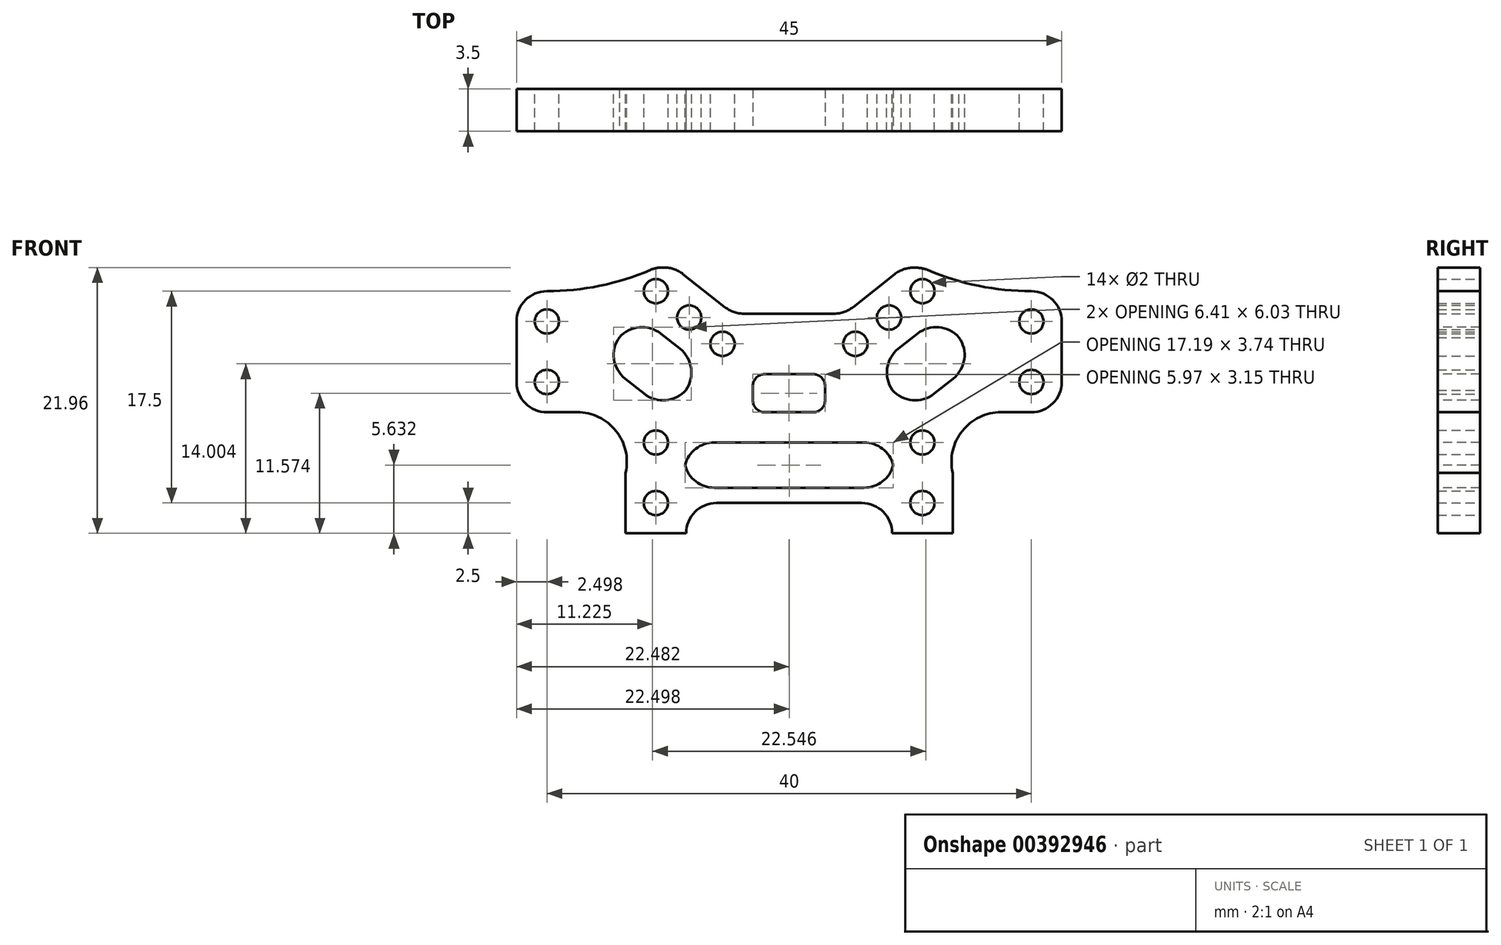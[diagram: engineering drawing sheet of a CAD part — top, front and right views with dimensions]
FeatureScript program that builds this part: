
annotation { "Feature Type Name" : "Feature", "Feature Type Description" : "" }
export const myFeature = defineFeature(function(context is Context, id is Id, definition is map)
    precondition{}
    {
        {
            var Q0;
            Q0=qCreatedBy(makeId("Front.planeOp"),FACE);
            var sketch = newSketch(context, id + "F0", { "sketchPlane" : qUnion([Q0])});
            skCircle(sketch, "E0", {"center": v(-2.32, 0) * mm, "radius": 1 * mm});
            skCircle(sketch, "E1", {"center": v(19.68, 0) * mm, "radius": 1 * mm});
            skCircle(sketch, "E2", {"center": v(-2.32, 5) * mm, "radius": 1 * mm});
            skCircle(sketch, "E3", {"center": v(19.68, 5) * mm, "radius": 1 * mm});
            skCircle(sketch, "E4", {"center": v(-11.32, 10) * mm, "radius": 1 * mm});
            skCircle(sketch, "E5", {"center": v(-11.32, 15) * mm, "radius": 1 * mm});
            skPoint(sketch, "E6.endSnap0", {"position": v(8.68, 5) * mm});
            skCircle(sketch, "E7.MirrorC", {"center": v(28.68, 15) * mm, "radius": 1 * mm});
            skCircle(sketch, "E8.MirrorC", {"center": v(28.68, 10) * mm, "radius": 1 * mm});
            skLineSegment(sketch, "E9", {"start": v(-4.82, 0) * mm, "end": v(-4.82, -2.5) * mm});
            skLineSegment(sketch, "E10", {"start": v(-4.82, -2.5) * mm, "end": v(0.18, -2.5) * mm});
            skLineSegment(sketch, "E11", {"start": v(0.18, -2.5) * mm, "end": v(0.18, 0) * mm});
            skLineSegment(sketch, "E12.trimOffspring", {"start": v(0.18, 0) * mm, "end": v(8.68, 0) * mm});
            skLineSegment(sketch, "E13.trimOffspring", {"start": v(18.68, 0) * mm, "end": v(19.68, 0) * mm});
            skLineSegment(sketch, "E14", {"start": v(-11.32, 10) * mm, "end": v(-13.82, 10) * mm});
            skLineSegment(sketch, "E15", {"start": v(-13.82, 10) * mm, "end": v(-13.82, 7.5) * mm});
            skLineSegment(sketch, "E16", {"start": v(-13.82, 7.5) * mm, "end": v(-8.82, 7.5) * mm});
            skLineSegment(sketch, "E17", {"start": v(-4.82, 0) * mm, "end": v(-4.82, 2.5) * mm});
            skArc(sketch, "E18", {"start": v(-4.82, 2.5) * mm, "mid": v(-5.62, 5.96) * mm, "end": v(-8.82, 7.5) * mm});
            skLineSegment(sketch, "E19", {"start": v(-11.32, 17.5) * mm, "end": v(-13.82, 17.5) * mm});
            skLineSegment(sketch, "E20", {"start": v(-13.82, 17.5) * mm, "end": v(-13.82, 10) * mm});
            skLineSegment(sketch, "E21.MirrorCS", {"start": v(28.68, 17.5) * mm, "end": v(31.18, 17.5) * mm});
            skLineSegment(sketch, "E22.MirrorCS", {"start": v(31.18, 17.5) * mm, "end": v(31.18, 10) * mm});
            skLineSegment(sketch, "E23.MirrorCS", {"start": v(31.18, 10) * mm, "end": v(31.18, 7.5) * mm});
            skLineSegment(sketch, "E24.MirrorCS", {"start": v(31.18, 7.5) * mm, "end": v(26.18, 7.5) * mm});
            skArc(sketch, "E25.MirrorCS", {"start": v(22.18, 2.5) * mm, "mid": v(22.98, 5.96) * mm, "end": v(26.18, 7.5) * mm});
            skLineSegment(sketch, "E26.MirrorCS", {"start": v(22.18, 0) * mm, "end": v(22.18, 2.5) * mm});
            skLineSegment(sketch, "E27.MirrorCS", {"start": v(22.18, 0) * mm, "end": v(22.18, -2.5) * mm});
            skLineSegment(sketch, "E28.MirrorCS", {"start": v(22.18, -2.5) * mm, "end": v(17.18, -2.5) * mm});
            skLineSegment(sketch, "E29.MirrorCS", {"start": v(17.18, 0) * mm, "end": v(8.68, 0) * mm});
            skLineSegment(sketch, "E30.MirrorCS", {"start": v(17.18, -2.5) * mm, "end": v(17.18, 0) * mm});
            skCircle(sketch, "E31", {"center": v(-2.32, 17.5) * mm, "radius": 1 * mm});
            skCircle(sketch, "E32.MirrorC", {"center": v(19.68, 17.5) * mm, "radius": 1 * mm});
            skCircle(sketch, "E33", {"center": v(3.18, 13.15) * mm, "radius": 1 * mm});
            skCircle(sketch, "E34", {"center": v(14.15, 13.15) * mm, "radius": 1 * mm});
            skCircle(sketch, "E35", {"center": v(16.93, 15.32) * mm, "radius": 1 * mm});
            skCircle(sketch, "E36", {"center": v(0.43, 15.32) * mm, "radius": 1 * mm});
            skLineSegment(sketch, "E37.0", {"start": v(13.28, 15.65) * mm, "end": v(18.07, 19.44) * mm});
            skLineSegment(sketch, "E37.1", {"start": v(4.05, 15.65) * mm, "end": v(13.28, 15.65) * mm});
            skLineSegment(sketch, "E37.2", {"start": v(-0.77, 19.46) * mm, "end": v(4.05, 15.65) * mm});
            skLineSegment(sketch, "E38", {"start": v(-0.77, 19.46) * mm, "end": v(-2.32, 19.46) * mm});
            skLineSegment(sketch, "E39", {"start": v(18.07, 19.44) * mm, "end": v(19.68, 19.44) * mm});
            skArc(sketch, "E40", {"start": v(19.68, 19.44) * mm, "mid": v(24.07, 18) * mm, "end": v(28.68, 17.5) * mm});
            skArc(sketch, "E41", {"start": v(-11.32, 17.5) * mm, "mid": v(-6.72, 18) * mm, "end": v(-2.32, 19.46) * mm});
            skSolve(sketch);
        }
        {
            var Q0;
            Q0 = qSketchRegion(id + "F0", true);
            extrude(context, id + "F1", {"entities" : qUnion([Q0]), "depth" : 3.5 * mm});
        }
        {
            var Q0;
            Q0=makeQuery(id+"F1.opExtrude","SWEPT_EDGE",EDGE,{"disambiguationData":[OSD([sQuery(id+"F0.wireOp",EDGE,"E19"),sQuery(id+"F0.wireOp",EDGE,"E20")])]});
            var Q1;
            Q1=makeQuery(id+"F1.opExtrude","SWEPT_EDGE",EDGE,{"disambiguationData":[OSD([sQuery(id+"F0.wireOp",EDGE,"E15"),sQuery(id+"F0.wireOp",EDGE,"E16")])]});
            var Q2;
            Q2=makeQuery(id+"F1.opExtrude","SWEPT_EDGE",EDGE,{"disambiguationData":[OSD([sQuery(id+"F0.wireOp",EDGE,"E23.MirrorCS"),sQuery(id+"F0.wireOp",EDGE,"E24.MirrorCS")])]});
            var Q3;
            Q3=makeQuery(id+"F1.opExtrude","SWEPT_EDGE",EDGE,{"disambiguationData":[OSD([sQuery(id+"F0.wireOp",EDGE,"E21.MirrorCS"),sQuery(id+"F0.wireOp",EDGE,"E22.MirrorCS")])]});
            var Q4;
            Q4=makeQuery(id+"F1.opExtrude","SWEPT_EDGE",EDGE,{"disambiguationData":[OSD([sQuery(id+"F0.wireOp",EDGE,"E38"),sQuery(id+"F0.wireOp",EDGE,"E41")])]});
            var Q5;
            Q5=makeQuery(id+"F1.opExtrude","SWEPT_EDGE",EDGE,{"disambiguationData":[OSD([sQuery(id+"F0.wireOp",EDGE,"E37.2"),sQuery(id+"F0.wireOp",EDGE,"E38")])]});
            var Q6;
            Q6=makeQuery(id+"F1.opExtrude","SWEPT_EDGE",EDGE,{"disambiguationData":[OSD([sQuery(id+"F0.wireOp",EDGE,"E37.1"),sQuery(id+"F0.wireOp",EDGE,"E37.2")])]});
            var Q7;
            Q7=makeQuery(id+"F1.opExtrude","SWEPT_EDGE",EDGE,{"disambiguationData":[OSD([sQuery(id+"F0.wireOp",EDGE,"E37.0"),sQuery(id+"F0.wireOp",EDGE,"E37.1")])]});
            var Q8;
            Q8=makeQuery(id+"F1.opExtrude","SWEPT_EDGE",EDGE,{"disambiguationData":[OSD([sQuery(id+"F0.wireOp",EDGE,"E37.0"),sQuery(id+"F0.wireOp",EDGE,"E39")])]});
            var Q9;
            Q9=makeQuery(id+"F1.opExtrude","SWEPT_EDGE",EDGE,{"disambiguationData":[OSD([sQuery(id+"F0.wireOp",EDGE,"E39"),sQuery(id+"F0.wireOp",EDGE,"E40")])]});
            var Q10;
            Q10=makeQuery(id+"F1.opExtrude","SWEPT_EDGE",EDGE,{"disambiguationData":[OSD([sQuery(id+"F0.wireOp",EDGE,"E11"),sQuery(id+"F0.wireOp",EDGE,"E12.trimOffspring")])]});
            var Q11;
            Q11=makeQuery(id+"F1.opExtrude","SWEPT_EDGE",EDGE,{"disambiguationData":[OSD([sQuery(id+"F0.wireOp",EDGE,"E29.MirrorCS"),sQuery(id+"F0.wireOp",EDGE,"E30.MirrorCS")])]});
            fillet(context, id + "F2", {"entities" : qUnion([Q0, Q1, Q2, Q3, Q4, Q5, Q6, Q7, Q8, Q9, Q10, Q11]), "radius" : 2.5 * mm, "tangentPropagation" : true, "allowEdgeOverflow" : false});
        }
        {
            var Q0;
            Q0=makeQuery(id+"F1.opExtrude","CAP_FACE",FACE,{"disambiguationData":[OSD([sQuery(id+"F0.wireOp",EDGE,"E0"),sQuery(id+"F0.wireOp",EDGE,"E1"),sQuery(id+"F0.wireOp",EDGE,"E2"),sQuery(id+"F0.wireOp",EDGE,"E3"),sQuery(id+"F0.wireOp",EDGE,"E4"),sQuery(id+"F0.wireOp",EDGE,"E5"),sQuery(id+"F0.wireOp",EDGE,"E7.MirrorC"),sQuery(id+"F0.wireOp",EDGE,"E8.MirrorC"),sQuery(id+"F0.wireOp",EDGE,"E9"),sQuery(id+"F0.wireOp",EDGE,"E10"),sQuery(id+"F0.wireOp",EDGE,"E11"),sQuery(id+"F0.wireOp",EDGE,"E12.trimOffspring"),sQuery(id+"F0.wireOp",EDGE,"E15"),sQuery(id+"F0.wireOp",EDGE,"E16"),sQuery(id+"F0.wireOp",EDGE,"E17"),sQuery(id+"F0.wireOp",EDGE,"E18"),sQuery(id+"F0.wireOp",EDGE,"E19"),sQuery(id+"F0.wireOp",EDGE,"E20"),sQuery(id+"F0.wireOp",EDGE,"E21.MirrorCS"),sQuery(id+"F0.wireOp",EDGE,"E22.MirrorCS"),sQuery(id+"F0.wireOp",EDGE,"E23.MirrorCS"),sQuery(id+"F0.wireOp",EDGE,"E24.MirrorCS"),sQuery(id+"F0.wireOp",EDGE,"E25.MirrorCS"),sQuery(id+"F0.wireOp",EDGE,"E26.MirrorCS"),sQuery(id+"F0.wireOp",EDGE,"E27.MirrorCS"),sQuery(id+"F0.wireOp",EDGE,"E28.MirrorCS"),sQuery(id+"F0.wireOp",EDGE,"E29.MirrorCS"),sQuery(id+"F0.wireOp",EDGE,"E30.MirrorCS"),sQuery(id+"F0.wireOp",EDGE,"E31"),sQuery(id+"F0.wireOp",EDGE,"E32.MirrorC"),sQuery(id+"F0.wireOp",EDGE,"E33"),sQuery(id+"F0.wireOp",EDGE,"E34"),sQuery(id+"F0.wireOp",EDGE,"E35"),sQuery(id+"F0.wireOp",EDGE,"E36"),sQuery(id+"F0.wireOp",EDGE,"E37.0"),sQuery(id+"F0.wireOp",EDGE,"E37.1"),sQuery(id+"F0.wireOp",EDGE,"E37.2"),sQuery(id+"F0.wireOp",EDGE,"E38"),sQuery(id+"F0.wireOp",EDGE,"E39"),sQuery(id+"F0.wireOp",EDGE,"E40"),sQuery(id+"F0.wireOp",EDGE,"E41")])],"isStart":false});
            var sketch = newSketch(context, id + "F3", { "sketchPlane" : qUnion([Q0])});
            skLineSegment(sketch, "E42", {"start": v(0, 5) * mm, "end": v(17.36, 5) * mm});
            skLineSegment(sketch, "E43", {"start": v(8.68, 5) * mm, "end": v(8.68, 1.26) * mm});
            skLineSegment(sketch, "E44", {"start": v(8.68, 1.26) * mm, "end": v(0, 1.26) * mm});
            skLineSegment(sketch, "E45", {"start": v(0, 1.26) * mm, "end": v(0, 5) * mm});
            skLineSegment(sketch, "E46.MirrorCS", {"start": v(8.68, 1.26) * mm, "end": v(17.36, 1.26) * mm});
            skLineSegment(sketch, "E47.MirrorCS", {"start": v(17.36, 1.26) * mm, "end": v(17.36, 5) * mm});
            skPoint(sketch, "E48.orphan", {"position": v(-2.32, 5) * mm});
            skPoint(sketch, "E49.orphan", {"position": v(19.68, 5) * mm});
            skLineSegment(sketch, "E50", {"start": v(-3.87, 15.54) * mm, "end": v(1.63, 11.19) * mm});
            skLineSegment(sketch, "E51", {"start": v(-3.87, 15.54) * mm, "end": v(-6.82, 11.82) * mm});
            skLineSegment(sketch, "E52", {"start": v(-6.82, 11.82) * mm, "end": v(-1.32, 7.47) * mm});
            skLineSegment(sketch, "E53.MirrorCS", {"start": v(21.23, 15.54) * mm, "end": v(15.73, 11.19) * mm});
            skLineSegment(sketch, "E54.MirrorCS", {"start": v(24.17, 11.82) * mm, "end": v(18.67, 7.47) * mm});
            skLineSegment(sketch, "E55.MirrorCS", {"start": v(21.23, 15.54) * mm, "end": v(24.17, 11.82) * mm});
            skLineSegment(sketch, "E56", {"start": v(1.63, 11.19) * mm, "end": v(-1.32, 7.47) * mm});
            skLineSegment(sketch, "E57", {"start": v(15.73, 11.19) * mm, "end": v(18.67, 7.47) * mm});
            skPoint(sketch, "E58.orphan", {"position": v(-1.28, 7.44) * mm});
            skPoint(sketch, "E59.orphan", {"position": v(18.63, 7.44) * mm});
            skSolve(sketch);
        }
        {
            var Q0;
            Q0=makeQuery(id+"F3.imprint","IMPRINT",FACE,{"disambiguationData":[TD([[makeQuery(id+"F3.imprint","IMPRINT",EDGE,{"derivedFrom":sQuery(id+"F3.wireOp",EDGE,"E50")}),-1.0]])]});
            var Q1;
            {var subQ2=sQuery(id+"F3.wireOp",EDGE,"E43");Q1=makeQuery(id+"F3.imprint","IMPRINT",FACE,{"disambiguationData":[TD([[makeQuery(id+"F3.imprint","IMPRINT",EDGE,{"derivedFrom":subQ2}),-1.0]])]});}
            var Q2;
            {var subQ2=sQuery(id+"F3.wireOp",EDGE,"E43");Q2=makeQuery(id+"F3.imprint","IMPRINT",FACE,{"disambiguationData":[TD([[makeQuery(id+"F3.imprint","IMPRINT",EDGE,{"derivedFrom":subQ2}),1.0]])]});}
            var Q3;
            Q3=makeQuery(id+"F3.imprint","IMPRINT",FACE,{"disambiguationData":[TD([[makeQuery(id+"F3.imprint","IMPRINT",EDGE,{"derivedFrom":sQuery(id+"F3.wireOp",EDGE,"E53.MirrorCS")}),1.0]])]});
            extrude(context, id + "F4", {"entities" : qUnion([Q0, Q1, Q2, Q3]), "operationType" : NewBodyOperationType.REMOVE, "oppositeDirection" : true, "depth" : 25.4 * mm});
        }
        {
            var Q0;
            Q0=makeQuery(id+"F4.boolean.opBoolean","COPY",EDGE,{"derivedFrom":makeQuery(id+"F4.opExtrude","SWEPT_EDGE",EDGE,{"disambiguationData":[OSD([sQuery(id+"F3.wireOp",EDGE,"E50"),sQuery(id+"F3.wireOp",EDGE,"E51")])]})});
            var Q1;
            Q1=makeQuery(id+"F4.boolean.opBoolean","COPY",EDGE,{"derivedFrom":makeQuery(id+"F4.opExtrude","SWEPT_EDGE",EDGE,{"disambiguationData":[OSD([sQuery(id+"F3.wireOp",EDGE,"E51"),sQuery(id+"F3.wireOp",EDGE,"E52")])]})});
            var Q2;
            Q2=makeQuery(id+"F4.boolean.opBoolean","COPY",EDGE,{"derivedFrom":makeQuery(id+"F4.opExtrude","SWEPT_EDGE",EDGE,{"disambiguationData":[OSD([sQuery(id+"F3.wireOp",EDGE,"E52"),sQuery(id+"F3.wireOp",EDGE,"E56")])]})});
            var Q3;
            Q3=makeQuery(id+"F4.boolean.opBoolean","COPY",EDGE,{"derivedFrom":makeQuery(id+"F4.opExtrude","SWEPT_EDGE",EDGE,{"disambiguationData":[OSD([sQuery(id+"F3.wireOp",EDGE,"E50"),sQuery(id+"F3.wireOp",EDGE,"E56")])]})});
            var Q4;
            Q4=makeQuery(id+"F4.boolean.opBoolean","COPY",EDGE,{"derivedFrom":makeQuery(id+"F4.opExtrude","SWEPT_EDGE",EDGE,{"disambiguationData":[OSD([sQuery(id+"F3.wireOp",EDGE,"E54.MirrorCS"),sQuery(id+"F3.wireOp",EDGE,"E55.MirrorCS")])]})});
            var Q5;
            Q5=makeQuery(id+"F4.boolean.opBoolean","COPY",EDGE,{"derivedFrom":makeQuery(id+"F4.opExtrude","SWEPT_EDGE",EDGE,{"disambiguationData":[OSD([sQuery(id+"F3.wireOp",EDGE,"E53.MirrorCS"),sQuery(id+"F3.wireOp",EDGE,"E55.MirrorCS")])]})});
            var Q6;
            Q6=makeQuery(id+"F4.boolean.opBoolean","COPY",EDGE,{"derivedFrom":makeQuery(id+"F4.opExtrude","SWEPT_EDGE",EDGE,{"disambiguationData":[OSD([sQuery(id+"F3.wireOp",EDGE,"E53.MirrorCS"),sQuery(id+"F3.wireOp",EDGE,"E57")])]})});
            var Q7;
            Q7=makeQuery(id+"F4.boolean.opBoolean","COPY",EDGE,{"derivedFrom":makeQuery(id+"F4.opExtrude","SWEPT_EDGE",EDGE,{"disambiguationData":[OSD([sQuery(id+"F3.wireOp",EDGE,"E54.MirrorCS"),sQuery(id+"F3.wireOp",EDGE,"E57")])]})});
            var Q8;
            Q8=makeQuery(id+"F4.boolean.opBoolean","COPY",EDGE,{"derivedFrom":makeQuery(id+"F4.opExtrude","SWEPT_EDGE",EDGE,{"disambiguationData":[OSD([sQuery(id+"F3.wireOp",EDGE,"E44"),sQuery(id+"F3.wireOp",EDGE,"E45")])]})});
            var Q9;
            Q9=makeQuery(id+"F4.boolean.opBoolean","COPY",EDGE,{"derivedFrom":makeQuery(id+"F4.opExtrude","SWEPT_EDGE",EDGE,{"disambiguationData":[OSD([sQuery(id+"F3.wireOp",EDGE,"E42"),sQuery(id+"F3.wireOp",EDGE,"E45")])]})});
            var Q10;
            Q10=makeQuery(id+"F4.boolean.opBoolean","COPY",EDGE,{"derivedFrom":makeQuery(id+"F4.opExtrude","SWEPT_EDGE",EDGE,{"disambiguationData":[OSD([sQuery(id+"F3.wireOp",EDGE,"E42"),sQuery(id+"F3.wireOp",EDGE,"E47.MirrorCS")])]})});
            var Q11;
            Q11=makeQuery(id+"F4.boolean.opBoolean","COPY",EDGE,{"derivedFrom":makeQuery(id+"F4.opExtrude","SWEPT_EDGE",EDGE,{"disambiguationData":[OSD([sQuery(id+"F3.wireOp",EDGE,"E46.MirrorCS"),sQuery(id+"F3.wireOp",EDGE,"E47.MirrorCS")])]})});
            fillet(context, id + "F5", {"entities" : qUnion([Q0, Q1, Q2, Q3, Q4, Q5, Q6, Q7, Q8, Q9, Q10, Q11]), "radius" : 2.5 * mm, "tangentPropagation" : true, "allowEdgeOverflow" : false});
        }
        {
            var Q0;
            Q0=makeQuery(id+"F1.opExtrude","CAP_FACE",FACE,{"disambiguationData":[OSD([sQuery(id+"F0.wireOp",EDGE,"E0"),sQuery(id+"F0.wireOp",EDGE,"E1"),sQuery(id+"F0.wireOp",EDGE,"E2"),sQuery(id+"F0.wireOp",EDGE,"E3"),sQuery(id+"F0.wireOp",EDGE,"E4"),sQuery(id+"F0.wireOp",EDGE,"E5"),sQuery(id+"F0.wireOp",EDGE,"E7.MirrorC"),sQuery(id+"F0.wireOp",EDGE,"E8.MirrorC"),sQuery(id+"F0.wireOp",EDGE,"E9"),sQuery(id+"F0.wireOp",EDGE,"E10"),sQuery(id+"F0.wireOp",EDGE,"E11"),sQuery(id+"F0.wireOp",EDGE,"E12.trimOffspring"),sQuery(id+"F0.wireOp",EDGE,"E15"),sQuery(id+"F0.wireOp",EDGE,"E16"),sQuery(id+"F0.wireOp",EDGE,"E17"),sQuery(id+"F0.wireOp",EDGE,"E18"),sQuery(id+"F0.wireOp",EDGE,"E19"),sQuery(id+"F0.wireOp",EDGE,"E20"),sQuery(id+"F0.wireOp",EDGE,"E21.MirrorCS"),sQuery(id+"F0.wireOp",EDGE,"E22.MirrorCS"),sQuery(id+"F0.wireOp",EDGE,"E23.MirrorCS"),sQuery(id+"F0.wireOp",EDGE,"E24.MirrorCS"),sQuery(id+"F0.wireOp",EDGE,"E25.MirrorCS"),sQuery(id+"F0.wireOp",EDGE,"E26.MirrorCS"),sQuery(id+"F0.wireOp",EDGE,"E27.MirrorCS"),sQuery(id+"F0.wireOp",EDGE,"E28.MirrorCS"),sQuery(id+"F0.wireOp",EDGE,"E29.MirrorCS"),sQuery(id+"F0.wireOp",EDGE,"E30.MirrorCS"),sQuery(id+"F0.wireOp",EDGE,"E31"),sQuery(id+"F0.wireOp",EDGE,"E32.MirrorC"),sQuery(id+"F0.wireOp",EDGE,"E33"),sQuery(id+"F0.wireOp",EDGE,"E34"),sQuery(id+"F0.wireOp",EDGE,"E35"),sQuery(id+"F0.wireOp",EDGE,"E36"),sQuery(id+"F0.wireOp",EDGE,"E37.0"),sQuery(id+"F0.wireOp",EDGE,"E37.1"),sQuery(id+"F0.wireOp",EDGE,"E37.2"),sQuery(id+"F0.wireOp",EDGE,"E38"),sQuery(id+"F0.wireOp",EDGE,"E39"),sQuery(id+"F0.wireOp",EDGE,"E40"),sQuery(id+"F0.wireOp",EDGE,"E41")])],"isStart":false});
            var sketch = newSketch(context, id + "F6", { "sketchPlane" : qUnion([Q0])});
            skLineSegment(sketch, "E60.0", {"start": v(5.68, 10.65) * mm, "end": v(5.68, 7.5) * mm});
            skLineSegment(sketch, "E60.1", {"start": v(5.68, 10.65) * mm, "end": v(11.65, 10.65) * mm});
            skLineSegment(sketch, "E60.2", {"start": v(11.65, 10.65) * mm, "end": v(11.65, 7.5) * mm});
            skLineSegment(sketch, "E60.3", {"start": v(11.65, 7.5) * mm, "end": v(5.68, 7.5) * mm});
            skSolve(sketch);
        }
        {
            var Q0;
            Q0=makeQuery(id+"F6.imprint","IMPRINT",FACE,{"disambiguationData":[TD([[makeQuery(id+"F6.imprint","IMPRINT",EDGE,{"derivedFrom":sQuery(id+"F6.wireOp",EDGE,"E60.0")}),1.0]])]});
            extrude(context, id + "F7", {"entities" : qUnion([Q0]), "operationType" : NewBodyOperationType.REMOVE, "oppositeDirection" : true, "depth" : 25.4 * mm});
        }
        {
            var Q0;
            Q0=makeQuery(id+"F7.boolean.opBoolean","COPY",EDGE,{"derivedFrom":makeQuery(id+"F7.opExtrude","SWEPT_EDGE",EDGE,{"disambiguationData":[OSD([sQuery(id+"F6.wireOp",EDGE,"E60.0"),sQuery(id+"F6.wireOp",EDGE,"E60.3")])]})});
            var Q1;
            Q1=makeQuery(id+"F7.boolean.opBoolean","COPY",EDGE,{"derivedFrom":makeQuery(id+"F7.opExtrude","SWEPT_EDGE",EDGE,{"disambiguationData":[OSD([sQuery(id+"F6.wireOp",EDGE,"E60.0"),sQuery(id+"F6.wireOp",EDGE,"E60.1")])]})});
            var Q2;
            Q2=makeQuery(id+"F7.boolean.opBoolean","COPY",EDGE,{"derivedFrom":makeQuery(id+"F7.opExtrude","SWEPT_EDGE",EDGE,{"disambiguationData":[OSD([sQuery(id+"F6.wireOp",EDGE,"E60.2"),sQuery(id+"F6.wireOp",EDGE,"E60.3")])]})});
            var Q3;
            Q3=makeQuery(id+"F7.boolean.opBoolean","COPY",EDGE,{"derivedFrom":makeQuery(id+"F7.opExtrude","SWEPT_EDGE",EDGE,{"disambiguationData":[OSD([sQuery(id+"F6.wireOp",EDGE,"E60.1"),sQuery(id+"F6.wireOp",EDGE,"E60.2")])]})});
            fillet(context, id + "F8", {"entities" : qUnion([Q0, Q1, Q2, Q3]), "radius" : 1 * mm, "tangentPropagation" : true, "allowEdgeOverflow" : false});
        }
    });
